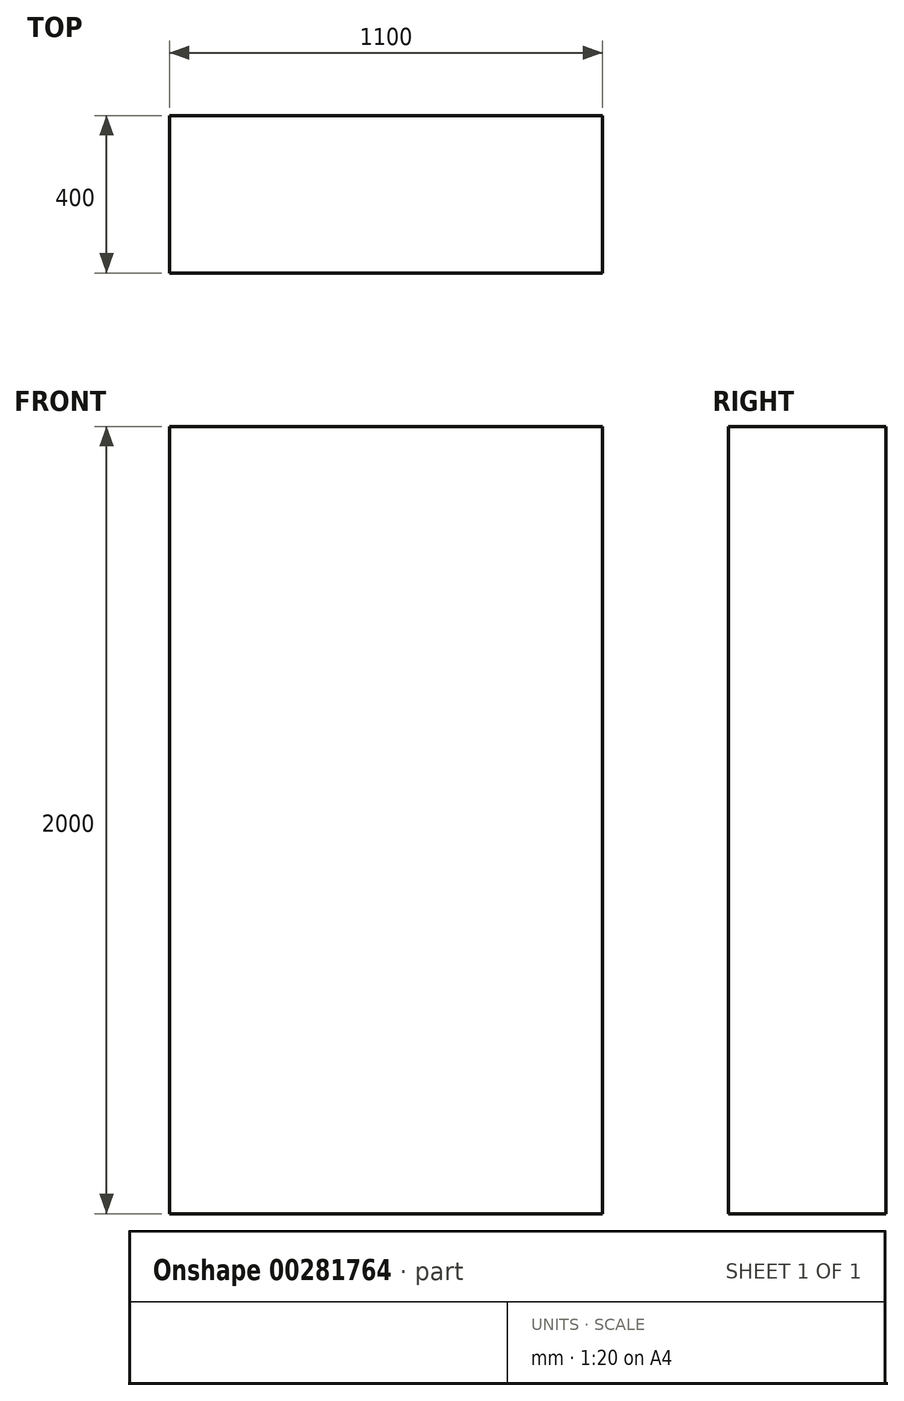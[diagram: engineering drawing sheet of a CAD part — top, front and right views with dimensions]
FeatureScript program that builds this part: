
annotation { "Feature Type Name" : "Feature", "Feature Type Description" : "" }
export const myFeature = defineFeature(function(context is Context, id is Id, definition is map)
    precondition{}
    {
        {
            var Q0;
            Q0=qCreatedBy(makeId("Front.planeOp"),FACE);
            var sketch = newSketch(context, id + "F0", { "sketchPlane" : qUnion([Q0])});
            skLineSegment(sketch, "E0.bottom", {"start": v(0, 0) * mm, "end": v(1100, 0) * mm});
            skLineSegment(sketch, "E0.top", {"start": v(0, 2000) * mm, "end": v(1100, 2000) * mm});
            skLineSegment(sketch, "E0.left", {"start": v(0, 0) * mm, "end": v(0, 2000) * mm});
            skLineSegment(sketch, "E0.right", {"start": v(1100, 0) * mm, "end": v(1100, 2000) * mm});
            skSolve(sketch);
        }
        {
            var Q0;
            Q0=makeQuery(id+"F0.imprint","IMPRINT",FACE,{"disambiguationData":[TD([[makeQuery(id+"F0.imprint","IMPRINT",EDGE,{"derivedFrom":sQuery(id+"F0.wireOp",EDGE,"E0.bottom")}),1.0]])]});
            extrude(context, id + "F1", {"entities" : qUnion([Q0]), "oppositeDirection" : true, "depth" : 400 * mm});
        }
    });
